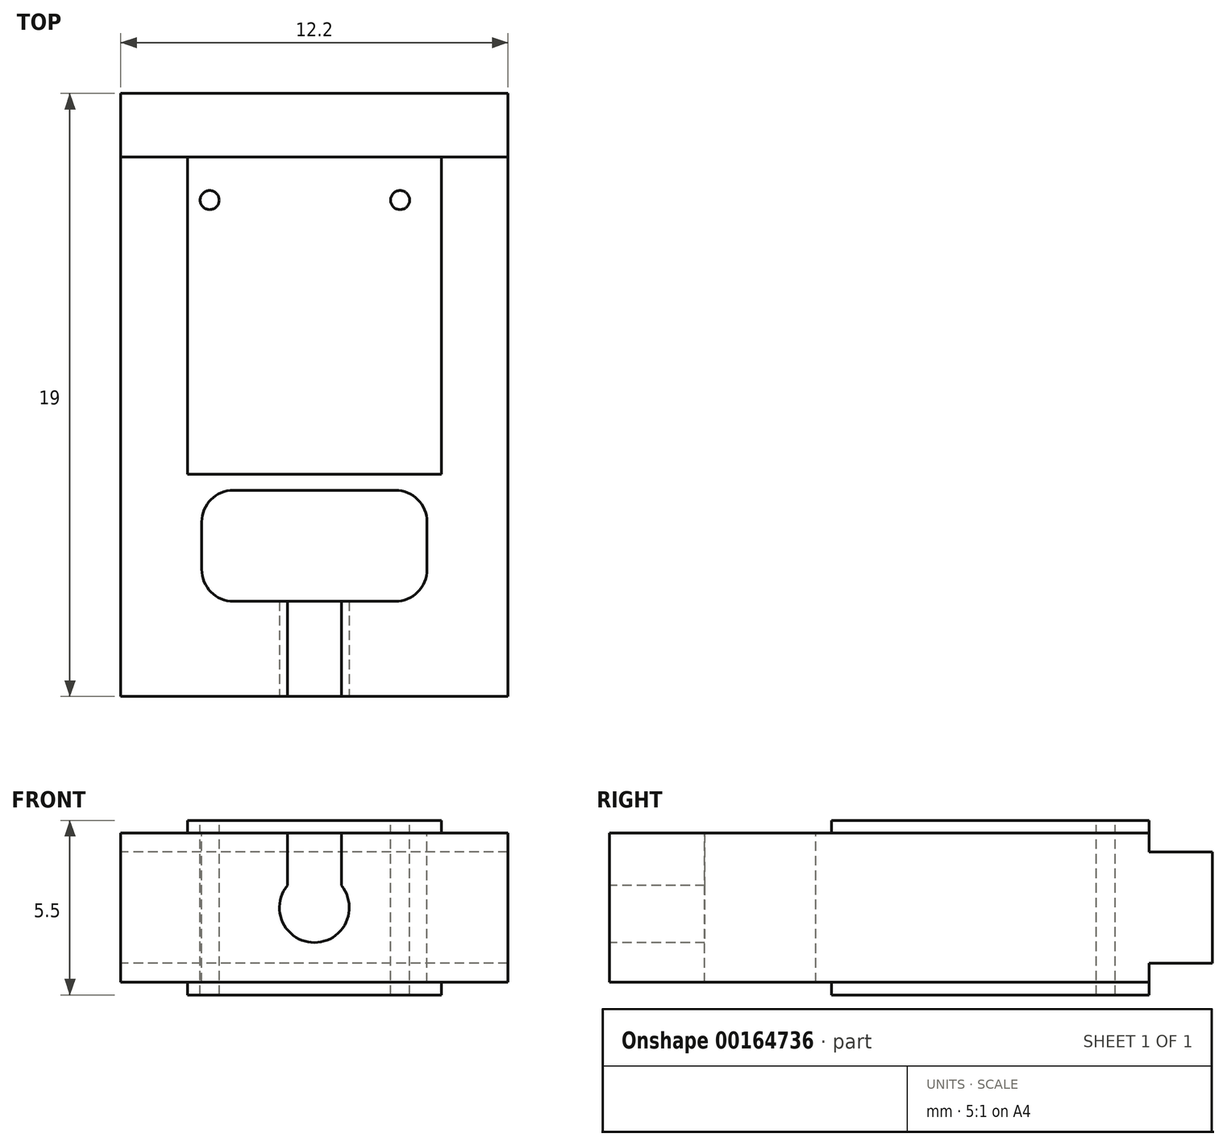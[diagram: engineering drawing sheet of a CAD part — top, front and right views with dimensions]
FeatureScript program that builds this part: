
annotation { "Feature Type Name" : "Feature", "Feature Type Description" : "" }
export const myFeature = defineFeature(function(context is Context, id is Id, definition is map)
    precondition{}
    {
        {
            assignVariable(context, id + "F0", {"name" : "Main_Width", "anyValue" : 12.2});
        }
        {
            assignVariable(context, id + "F1", {"name" : "Thickness1", "anyValue" : 4.7});
        }
        {
            assignVariable(context, id + "F2", {"name" : "Thickness2", "anyValue" : 5.5});
        }
        {
            var Q0;
            Q0=qCreatedBy(makeId("Right.planeOp"),FACE);
            var sketch = newSketch(context, id + "F3", { "sketchPlane" : qUnion([Q0])});
            skLineSegment(sketch, "E0", {"start": v(0, 0) * mm, "end": v(0, 2.35) * mm});
            skLineSegment(sketch, "E1", {"start": v(19, 1.75) * mm, "end": v(19, 0) * mm});
            skLineSegment(sketch, "E2", {"start": v(0, 0) * mm, "end": v(19, 0) * mm, "construction": true});
            skLineSegment(sketch, "E3.MirrorCS", {"start": v(0, -2.35) * mm, "end": v(17, -2.35) * mm});
            skLineSegment(sketch, "E4.MirrorCS", {"start": v(0, 0) * mm, "end": v(0, -2.35) * mm});
            skLineSegment(sketch, "E5.MirrorCS", {"start": v(19, -1.75) * mm, "end": v(19, 0) * mm});
            skLineSegment(sketch, "E6", {"start": v(0, 2.35) * mm, "end": v(17, 2.35) * mm});
            skLineSegment(sketch, "E7", {"start": v(19, 1.75) * mm, "end": v(17, 1.75) * mm});
            skLineSegment(sketch, "E8", {"start": v(19, -1.75) * mm, "end": v(17, -1.75) * mm});
            skLineSegment(sketch, "E9", {"start": v(17, 2.35) * mm, "end": v(17, 1.75) * mm});
            skLineSegment(sketch, "E10", {"start": v(17, -1.75) * mm, "end": v(17, -2.35) * mm});
            skSolve(sketch);
        }
        {
            var Q0;
            Q0=makeQuery(id+"F3.imprint","IMPRINT",FACE,{"disambiguationData":[TD([[makeQuery(id+"F3.imprint","IMPRINT",EDGE,{"derivedFrom":sQuery(id+"F3.wireOp",EDGE,"E0")}),-1.0]])]});
            extrude(context, id + "F4", {"entities" : qUnion([Q0]), "depth" : (getVariable(context, 'Main_Width')) * mm});
        }
        {
            var Q0;
            Q0=makeQuery(id+"F4.opExtrude","SWEPT_FACE",FACE,{"disambiguationData":[OSD([sQuery(id+"F3.wireOp",EDGE,"E6")])]});
            cPlane(context, id + "F5", {"entities" : qUnion([Q0]), "cplaneType" : CPlaneType.OFFSET, "offset" : ((getVariable(context, 'Thickness2') - getVariable(context, 'Thickness1')) / 2) * mm, "width" : 150 * mm, "height" : 150 * mm});
        }
        {
            var Q0;
            Q0=qCreatedBy(id+"F5.planeOp",FACE);
            var sketch = newSketch(context, id + "F6", { "sketchPlane" : qUnion([Q0])});
            skLineSegment(sketch, "E11.bottom", {"start": v(2.1, 17) * mm, "end": v(10.1, 17) * mm});
            skLineSegment(sketch, "E11.top", {"start": v(2.1, 7) * mm, "end": v(10.1, 7) * mm});
            skLineSegment(sketch, "E11.left", {"start": v(2.1, 17) * mm, "end": v(2.1, 7) * mm});
            skLineSegment(sketch, "E11.right", {"start": v(10.1, 17) * mm, "end": v(10.1, 7) * mm});
            skPoint(sketch, "E11.middle", {"position": v(6.1, 12) * mm});
            skPoint(sketch, "E12", {"position": v(6.1, 17) * mm});
            skLineSegment(sketch, "E13.0", {"start": v(12.2, 19) * mm, "end": v(0, 19) * mm});
            skPoint(sketch, "E14", {"position": v(6.1, 19) * mm});
            skSolve(sketch);
        }
        {
            var Q0;
            Q0=makeQuery(id+"F6.imprint","IMPRINT",FACE,{"disambiguationData":[TD([[makeQuery(id+"F6.imprint","IMPRINT",EDGE,{"derivedFrom":sQuery(id+"F6.wireOp",EDGE,"E11.bottom")}),-1.0]])]});
            extrude(context, id + "F7", {"entities" : qUnion([Q0]), "operationType" : NewBodyOperationType.ADD, "oppositeDirection" : true, "depth" : (getVariable(context, 'Thickness2')) * mm});
        }
        {
            var Q0;
            Q0=qCreatedBy(id+"F5.planeOp",FACE);
            var sketch = newSketch(context, id + "F8", { "sketchPlane" : qUnion([Q0])});
            skLineSegment(sketch, "E15.0", {"start": v(12.2, 0) * mm, "end": v(0, 0) * mm});
            skLineSegment(sketch, "E16", {"start": v(6.1, 15.64) * mm, "end": v(6.1, 0) * mm, "construction": true});
            skPoint(sketch, "E16.endSnap0", {"position": v(6.1, 0) * mm});
            skLineSegment(sketch, "E17.bottom", {"start": v(3.55, 3) * mm, "end": v(8.65, 3) * mm});
            skLineSegment(sketch, "E17.top", {"start": v(3.55, 6.5) * mm, "end": v(8.65, 6.5) * mm});
            skLineSegment(sketch, "E17.left", {"start": v(3.55, 3) * mm, "end": v(3.55, 6.5) * mm, "construction": true});
            skLineSegment(sketch, "E17.right", {"start": v(8.65, 3) * mm, "end": v(8.65, 6.5) * mm, "construction": true});
            skPoint(sketch, "E17.middle", {"position": v(6.1, 4.75) * mm});
            skArc(sketch, "E18", {"start": v(2.55, 4) * mm, "mid": v(2.84, 3.3) * mm, "end": v(3.55, 3) * mm});
            skArc(sketch, "E19", {"start": v(3.55, 6.5) * mm, "mid": v(2.84, 6.2) * mm, "end": v(2.55, 5.5) * mm});
            skLineSegment(sketch, "E20", {"start": v(2.55, 4) * mm, "end": v(2.55, 5.5) * mm});
            skArc(sketch, "E21.MirrorCS", {"start": v(8.65, 6.5) * mm, "mid": v(9.36, 6.2) * mm, "end": v(9.65, 5.5) * mm});
            skLineSegment(sketch, "E22.MirrorCS", {"start": v(9.65, 4) * mm, "end": v(9.65, 5.5) * mm});
            skArc(sketch, "E23.MirrorCS", {"start": v(9.65, 4) * mm, "mid": v(9.36, 3.3) * mm, "end": v(8.65, 3) * mm});
            skCircle(sketch, "E24", {"center": v(2.8, 15.64) * mm, "radius": 0.3 * mm});
            skCircle(sketch, "E25", {"center": v(8.8, 15.64) * mm, "radius": 0.3 * mm});
            skSolve(sketch);
        }
        {
            var Q0;
            Q0=makeQuery(id+"F8.imprint","IMPRINT",FACE,{"disambiguationData":[TD([[makeQuery(id+"F8.imprint","IMPRINT",EDGE,{"derivedFrom":sQuery(id+"F8.wireOp",EDGE,"E17.bottom")}),1.0]])]});
            var Q1;
            Q1=makeQuery(id+"F8.imprint","IMPRINT",FACE,{"disambiguationData":[TD([[makeQuery(id+"F8.imprint","IMPRINT",EDGE,{"derivedFrom":sQuery(id+"F8.wireOp",EDGE,"E24")}),1.0]])]});
            var Q2;
            Q2=makeQuery(id+"F8.imprint","IMPRINT",FACE,{"disambiguationData":[TD([[makeQuery(id+"F8.imprint","IMPRINT",EDGE,{"derivedFrom":sQuery(id+"F8.wireOp",EDGE,"E25")}),1.0]])]});
            extrude(context, id + "F9", {"entities" : qUnion([Q0, Q1, Q2]), "operationType" : NewBodyOperationType.REMOVE, "endBound" : BoundingType.THROUGH_ALL, "oppositeDirection" : true, "depth" : 25 * mm});
        }
        {
            var Q0;
            Q0=makeQuery(id+"F4.opExtrude","SWEPT_FACE",FACE,{"disambiguationData":[OSD([sQuery(id+"F3.wireOp",EDGE,"E0"),sQuery(id+"F3.wireOp",EDGE,"E4.MirrorCS")])]});
            var sketch = newSketch(context, id + "F10", { "sketchPlane" : qUnion([Q0])});
            skLineSegment(sketch, "E26.0.0", {"start": v(0, 2.35) * mm, "end": v(0, -2.35) * mm});
            skLineSegment(sketch, "E26.0.1", {"start": v(0, -2.35) * mm, "end": v(12.2, -2.35) * mm});
            skLineSegment(sketch, "E26.0.2", {"start": v(12.2, -2.35) * mm, "end": v(12.2, 2.35) * mm});
            skLineSegment(sketch, "E26.0.3", {"start": v(12.2, 2.35) * mm, "end": v(0, 2.35) * mm});
            skArc(sketch, "E27", {"start": v(5.25, 0.7) * mm, "mid": v(6.1, -1.1) * mm, "end": v(6.95, 0.7) * mm});
            skLineSegment(sketch, "E28", {"start": v(6.1, 2.35) * mm, "end": v(6.1, -2.35) * mm, "construction": true});
            skLineSegment(sketch, "E29", {"start": v(5.25, 0.7) * mm, "end": v(5.25, 2.35) * mm});
            skLineSegment(sketch, "E30", {"start": v(6.95, 0.7) * mm, "end": v(6.95, 2.35) * mm});
            skSolve(sketch);
        }
        {
            var Q0;
            Q0=makeQuery(id+"F10.imprint","IMPRINT",FACE,{"disambiguationData":[TD([[makeQuery(id+"F10.imprint","IMPRINT",EDGE,{"derivedFrom":sQuery(id+"F10.wireOp",EDGE,"E27")}),1.0]])]});
            extrude(context, id + "F11", {"entities" : qUnion([Q0]), "operationType" : NewBodyOperationType.REMOVE, "endBound" : BoundingType.UP_TO_NEXT, "oppositeDirection" : true, "depth" : 25 * mm});
        }
    });
